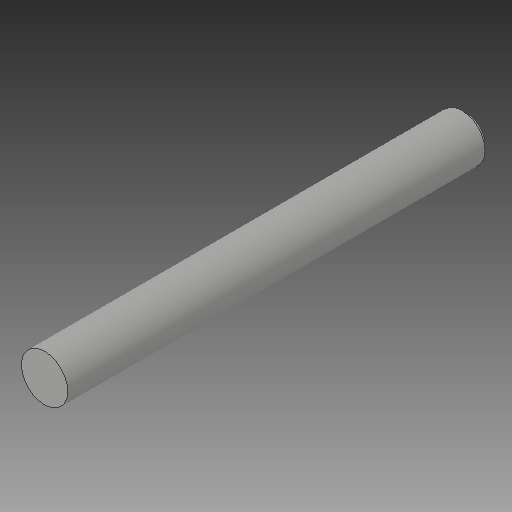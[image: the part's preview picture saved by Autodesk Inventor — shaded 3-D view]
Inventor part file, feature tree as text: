
AUTODESK INVENTOR PART (.ipt)
format: ipt  version: 2018 (Build 220112000, 112)  size: 115,712 bytes
history: native  units: mm
features: other x1, extrude x1, chamfer x1, sketch x1
ambient origin geometry x8: Origin, YZ Plane, XZ Plane, XY Plane, X Axis, Y Axis, Z Axis, Center Point
bodies: Solid1 (feature_tree)
feature tree (4):
  parser-record x1  (decoder bookkeeping rows leaked as tree rows — omitted from the tree; the rows remain in map.json)
  extrude  "Extrusion1"  Depth=228.0mm
  chamfer  "Chamfer1"  [1 undecoded]
  sketch  "Sketch1"  dims[d0=25.0mm d1=228.0mm d2=0.0mm d3=3.0mm d4=2.0mm d5=45.0deg]
note: 1 required parameter value undecoded (feature->parameter linkage not recoverable at this tier; creation-order binding heuristic only, values carry confidence <= 0.55)
note: 1 file-system path scrubbed to <path> (originals preserved in map.json)
